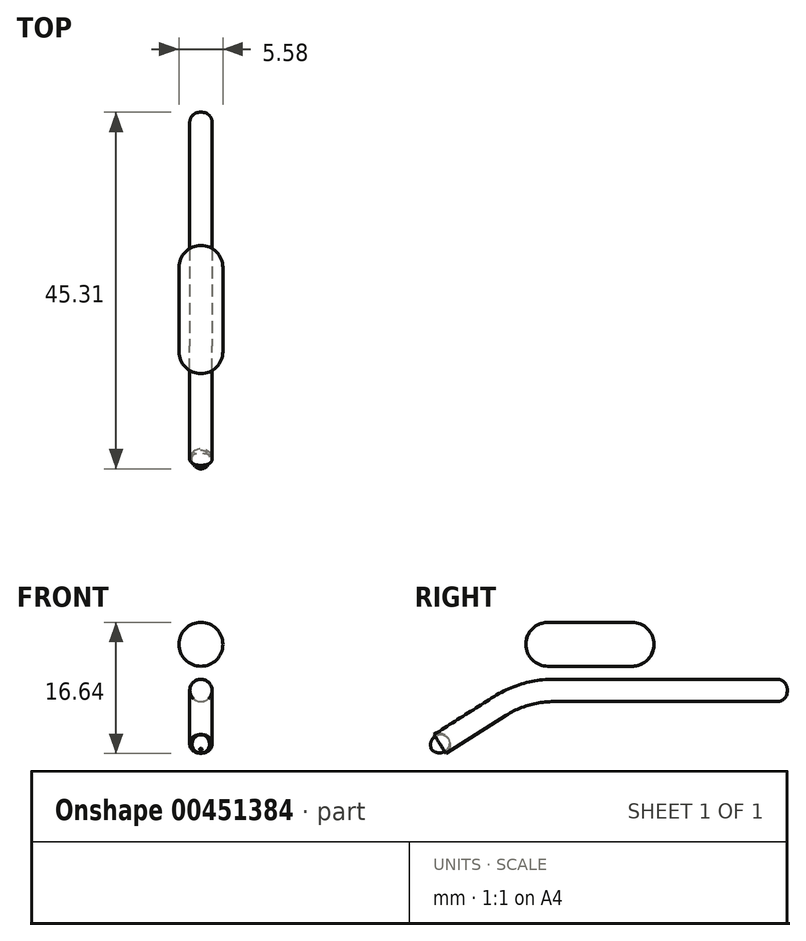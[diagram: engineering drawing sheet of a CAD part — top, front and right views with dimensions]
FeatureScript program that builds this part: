
annotation { "Feature Type Name" : "Feature", "Feature Type Description" : "" }
export const myFeature = defineFeature(function(context is Context, id is Id, definition is map)
    precondition{}
    {
        {
            var Q0;
            Q0=qCreatedBy(makeId("Right.planeOp"),FACE);
            var sketch = newSketch(context, id + "F0", { "sketchPlane" : qUnion([Q0])});
            skLineSegment(sketch, "E0", {"start": v(-23.95, -7.97) * mm, "end": v(-15.22, -2.46) * mm});
            skLineSegment(sketch, "E1", {"start": v(-8.44, -0.5) * mm, "end": v(21.24, -0.5) * mm});
            skPoint(sketch, "E2.visualSharp", {"position": v(-12.12, -0.5) * mm});
            skArc(sketch, "E2.filletArc", {"start": v(-8.44, -0.5) * mm, "mid": v(-11.97, -1) * mm, "end": v(-15.22, -2.46) * mm});
            skSolve(sketch);
        }
        {
            var Q0;
            Q0=sQuery(id+"F0.wireOp",EDGE,"E1");
            var Q1;
            Q1=sQuery(id+"F0.wireOp",VERTEX,"E1.end");
            cPlane(context, id + "F1", {"entities" : qUnion([Q0, Q1]), "cplaneType" : CPlaneType.CURVE_POINT, "offset" : 25.4 * mm, "width" : 152.4 * mm, "height" : 152.4 * mm});
        }
        {
            var Q0;
            Q0=qCreatedBy(id+"F1.planeOp",FACE);
            var sketch = newSketch(context, id + "F2", { "sketchPlane" : qUnion([Q0])});
            skCircle(sketch, "E3", {"center": v(0, -0.5) * mm, "radius": 1.42 * mm});
            skSolve(sketch);
        }
        {
            var Q0;
            Q0=makeQuery(id+"F2.imprint","IMPRINT",FACE,{"disambiguationData":[TD([[makeQuery(id+"F2.imprint","IMPRINT",EDGE,{"derivedFrom":sQuery(id+"F2.wireOp",EDGE,"E3")}),1.0]])]});
            var Q1;
            Q1=sQuery(id+"F0.wireOp",EDGE,"E1");
            var Q2;
            Q2=sQuery(id+"F0.wireOp",EDGE,"E2.filletArc");
            var Q3;
            Q3=sQuery(id+"F0.wireOp",EDGE,"E0");
            sweep(context, id + "F3", {"profiles" : qUnion([Q0]), "path" : qUnion([Q1, Q2, Q3])});
        }
        {
            var Q0;
            Q0=makeQuery(id+"F3.opSweep","CAP_EDGE",EDGE,{"disambiguationData":[OSD([sQuery(id+"F0.wireOp",VERTEX,"E1.end"),sQuery(id+"F2.wireOp",EDGE,"E3")])],"isStart":true});
            var Q1;
            Q1=makeQuery(id+"F3.opSweep","CAP_EDGE",EDGE,{"disambiguationData":[OSD([sQuery(id+"F0.wireOp",VERTEX,"E0.start"),sQuery(id+"F2.wireOp",EDGE,"E3")])],"isStart":false});
            fillet(context, id + "F4", {"entities" : qUnion([Q0, Q1]), "radius" : 1.27 * mm, "tangentPropagation" : true, "allowEdgeOverflow" : false});
        }
        {
            var Q0;
            Q0=qCreatedBy(makeId("Right.planeOp"),FACE);
            var sketch = newSketch(context, id + "F5", { "sketchPlane" : qUnion([Q0])});
            skLineSegment(sketch, "E4", {"start": v(7.49, 5.36) * mm, "end": v(-13.4, 5.36) * mm, "construction": true});
            skArc(sketch, "E5", {"start": v(4.3, 5.36) * mm, "mid": v(3.5, 7.33) * mm, "end": v(1.52, 8.15) * mm});
            skArc(sketch, "E6", {"start": v(-9.18, 8.15) * mm, "mid": v(-11.15, 7.33) * mm, "end": v(-11.96, 5.36) * mm});
            skLineSegment(sketch, "E7", {"start": v(1.52, 8.15) * mm, "end": v(-9.18, 8.15) * mm});
            skLineSegment(sketch, "E8", {"start": v(4.3, 5.36) * mm, "end": v(-11.96, 5.36) * mm});
            skSolve(sketch);
        }
        {
            var Q0;
            Q0=makeQuery(id+"F5.imprint","IMPRINT",FACE,{"disambiguationData":[TD([[makeQuery(id+"F5.imprint","IMPRINT",EDGE,{"derivedFrom":sQuery(id+"F5.wireOp",EDGE,"E5")}),1.0]])]});
            var Q1;
            Q1=sQuery(id+"F5.wireOp",EDGE,"E4");
            revolve(context, id + "F6", {"entities" : qUnion([Q0]), "axis" : qUnion([Q1]), "revolveType" : RevolveType.FULL});
        }
    });
